# Revit family: OKA-G Kanaleinheit für GES9, Höhe 40-240mm
name_source: partatom
category: Generic Models
revit_build: Autodesk Revit 2015 (Build: 20140606_1530(x64)
units: mm (PartAtom-declared; Revit-internal decimal feet)

## types (3) — shared parameters
Cut's number = 3
Manufacturer = OBO Bettermann
Material = Steel, Galvanized
URL = http://www.obo-bettermann.com

## per-type parameters (varying)
| type | Article Type | GTIN | Manufacturer Art. No. | Width |
| OKA-G40040240D9 | OKA-G40040240D9

OKA-G40040240D9

OKA-G40040240D9

OKA-G40040240D9

OKA-G40040240D9

OKA-G40040240D9

OKA-G40040240D9

OKA-G40040240D9

OKA-G40040240D9
v
OKA-G40040240D9

OKA-G40040240D9

OKA-G40040240D9

OKA-G40040240D9

OKA-G40040240D9
OKA-G40040240D9 | 4012195243687 | 7424220 | 400 mm  [stored 1.31234 ft] |
| OKA-G50040240D9 | OKA-G50040240D9 | 4012195243694

4012195243694
4012195243694 | 7424222

7424222

7424222

7424222

7424222

7424222

7424222
v
7424222

7424222

7424222
v
7424222

7424222
7424222 | 500 mm  [stored 1.64042 ft] |
| OKA-G60040240D9 | OKA-G60040240D9 | 4012195243700

4012195243700
4012195243700 | 7424224 | 600 mm |

note: [stored X ft] marks values corroborated as IEEE doubles in the binary element streams (Revit-internal decimal feet)

## geometry (parser evidence)
native form markers: Sweep x2
no freeform markers — native parametric forms only
